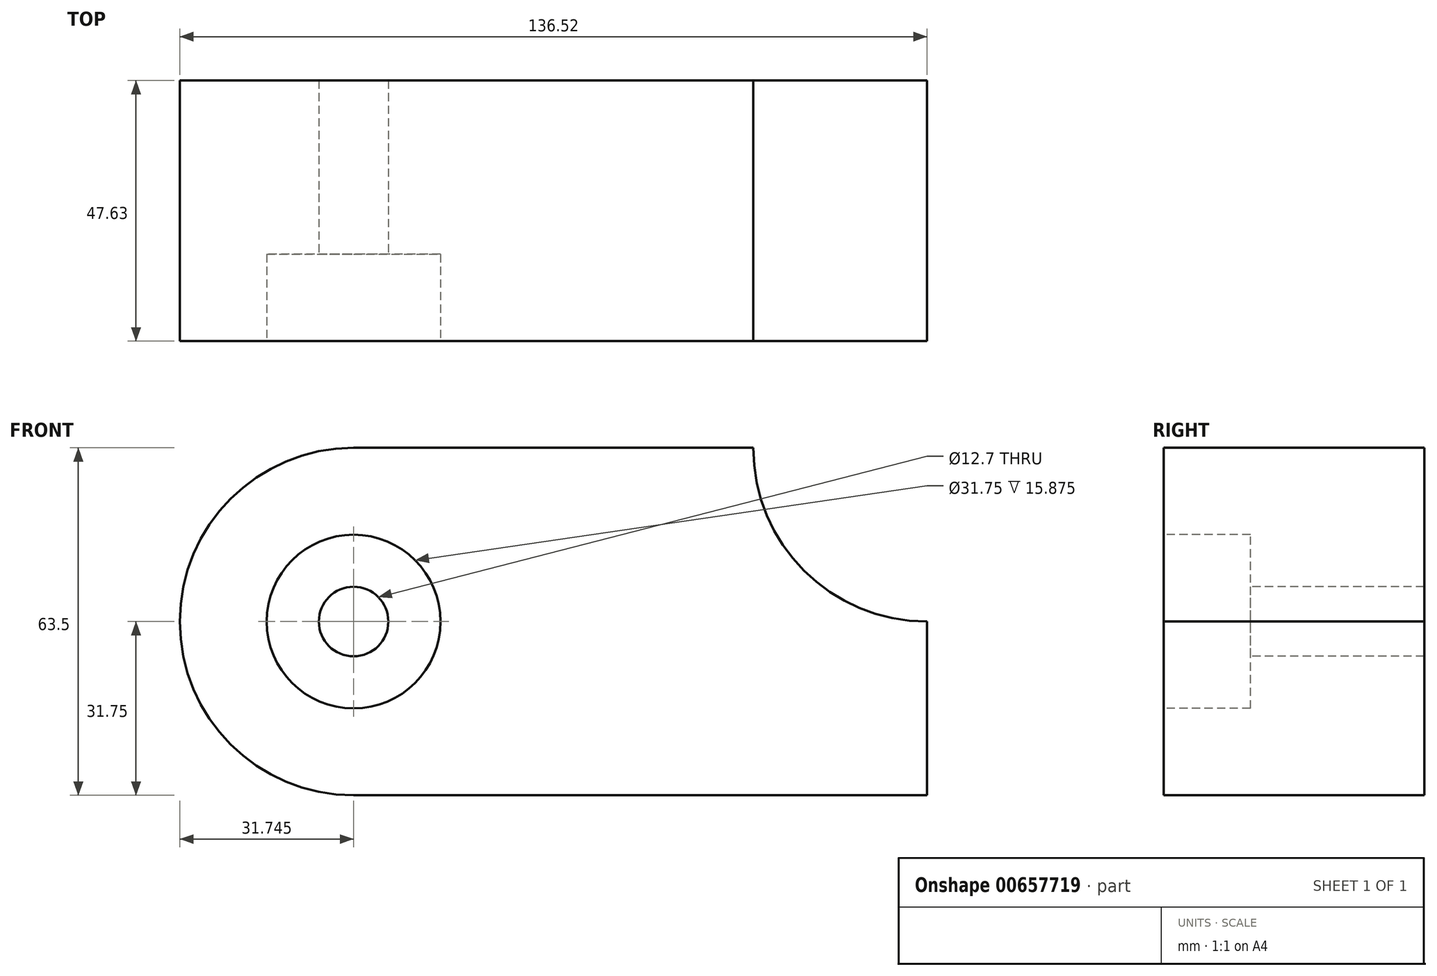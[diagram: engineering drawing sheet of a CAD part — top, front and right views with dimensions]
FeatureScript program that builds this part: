
annotation { "Feature Type Name" : "Feature", "Feature Type Description" : "" }
export const myFeature = defineFeature(function(context is Context, id is Id, definition is map)
    precondition{}
    {
        {
            var Q0;
            Q0=qCreatedBy(makeId("Front.planeOp"),FACE);
            var sketch = newSketch(context, id + "F0", { "sketchPlane" : qUnion([Q0])});
            skLineSegment(sketch, "E0", {"start": v(0, 0) * mm, "end": v(-104.77, 0) * mm});
            skLineSegment(sketch, "E1", {"start": v(-104.78, 0) * mm, "end": v(-104.78, 63.5) * mm});
            skLineSegment(sketch, "E2", {"start": v(-104.78, 63.5) * mm, "end": v(0, 63.5) * mm});
            skLineSegment(sketch, "E3", {"start": v(0, 63.5) * mm, "end": v(0, 0) * mm});
            skArc(sketch, "E4", {"start": v(-22.92, 41.53) * mm, "mid": v(-12.46, 34.3) * mm, "end": v(0, 31.75) * mm});
            skArc(sketch, "E5", {"start": v(-22.92, 41.53) * mm, "mid": v(-29.46, 51.66) * mm, "end": v(-31.75, 63.5) * mm});
            skArc(sketch, "E6", {"start": v(-104.78, 63.5) * mm, "mid": v(-136.53, 31.75) * mm, "end": v(-104.78, 0) * mm});
            skSolve(sketch);
        }
        {
            var Q0;
            Q0=makeQuery(id+"F0.imprint","IMPRINT",FACE,{"disambiguationData":[TD([[makeQuery(id+"F0.imprint","IMPRINT",EDGE,{"derivedFrom":sQuery(id+"F0.wireOp",EDGE,"E1")}),1.0]])]});
            var Q1;
            {var subQ4=sQuery(id+"F0.wireOp",EDGE,"E0");Q1=makeQuery(id+"F0.imprint","IMPRINT",FACE,{"disambiguationData":[TD([[makeQuery(id+"F0.imprint","IMPRINT",EDGE,{"derivedFrom":subQ4}),-1.0]])]});}
            extrude(context, id + "F1", {"entities" : qUnion([Q0, Q1]), "depth" : 47.62 * mm, "offsetDistance" : 25.4 * mm});
        }
        {
            var Q0;
            Q0=makeQuery(id+"F1.opExtrude","CAP_FACE",FACE,{"disambiguationData":[OSD([sQuery(id+"F0.wireOp",EDGE,"E0"),sQuery(id+"F0.wireOp",EDGE,"E2"),sQuery(id+"F0.wireOp",EDGE,"E3"),sQuery(id+"F0.wireOp",EDGE,"E4"),sQuery(id+"F0.wireOp",EDGE,"E5"),sQuery(id+"F0.wireOp",EDGE,"E6")])],"isStart":false});
            var sketch = newSketch(context, id + "F2", { "sketchPlane" : qUnion([Q0])});
            skCircle(sketch, "E7", {"center": v(-104.78, 31.75) * mm, "radius": 6.35 * mm});
            skCircle(sketch, "E8", {"center": v(-104.78, 31.75) * mm, "radius": 15.88 * mm});
            skSolve(sketch);
        }
        {
            var Q0;
            Q0=makeQuery(id+"F2.imprint","IMPRINT",FACE,{"disambiguationData":[TD([[makeQuery(id+"F2.imprint","IMPRINT",EDGE,{"derivedFrom":sQuery(id+"F2.wireOp",EDGE,"E7")}),1.0]])]});
            extrude(context, id + "F3", {"entities" : qUnion([Q0]), "operationType" : NewBodyOperationType.REMOVE, "oppositeDirection" : true, "depth" : 47.62 * mm, "offsetDistance" : 25.4 * mm});
        }
        {
            var Q0;
            Q0=makeQuery(id+"F1.opExtrude","CAP_FACE",FACE,{"disambiguationData":[OSD([sQuery(id+"F0.wireOp",EDGE,"E0"),sQuery(id+"F0.wireOp",EDGE,"E2"),sQuery(id+"F0.wireOp",EDGE,"E3"),sQuery(id+"F0.wireOp",EDGE,"E4"),sQuery(id+"F0.wireOp",EDGE,"E5"),sQuery(id+"F0.wireOp",EDGE,"E6")])],"isStart":false});
            var sketch = newSketch(context, id + "F4", { "sketchPlane" : qUnion([Q0])});
            skCircle(sketch, "E9", {"center": v(-104.78, 31.75) * mm, "radius": 15.88 * mm});
            skSolve(sketch);
        }
        {
            var Q0;
            Q0=makeQuery(id+"F4.imprint","IMPRINT",FACE,{"disambiguationData":[TD([[makeQuery(id+"F4.imprint","IMPRINT",EDGE,{"derivedFrom":sQuery(id+"F4.wireOp",EDGE,"E9")}),1.0]])]});
            extrude(context, id + "F5", {"entities" : qUnion([Q0]), "operationType" : NewBodyOperationType.REMOVE, "oppositeDirection" : true, "depth" : 15.88 * mm, "offsetDistance" : 25.4 * mm});
        }
    });
